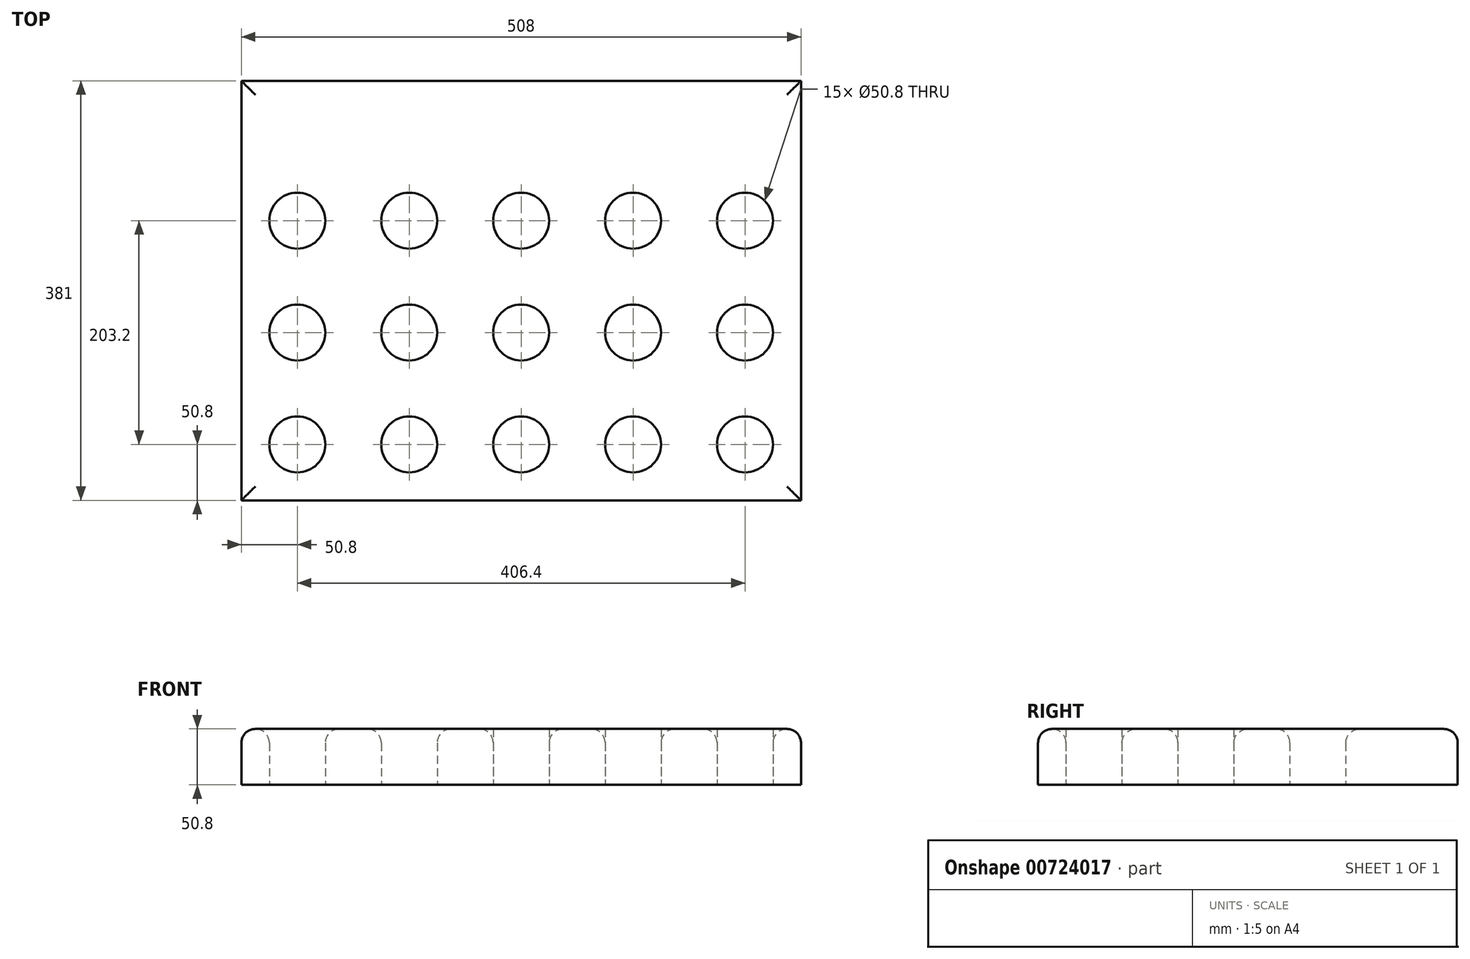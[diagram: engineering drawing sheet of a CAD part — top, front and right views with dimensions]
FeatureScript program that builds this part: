
annotation { "Feature Type Name" : "Feature", "Feature Type Description" : "" }
export const myFeature = defineFeature(function(context is Context, id is Id, definition is map)
    precondition{}
    {
        {
            var Q0;
            Q0=qCreatedBy(makeId("Top.planeOp"),FACE);
            var sketch = newSketch(context, id + "F0", { "sketchPlane" : qUnion([Q0])});
            skLineSegment(sketch, "E0.bottom", {"start": v(254, -190.5) * mm, "end": v(-254, -190.5) * mm});
            skLineSegment(sketch, "E0.top", {"start": v(254, 190.5) * mm, "end": v(-254, 190.5) * mm});
            skLineSegment(sketch, "E0.left", {"start": v(254, -190.5) * mm, "end": v(254, 190.5) * mm});
            skLineSegment(sketch, "E0.right", {"start": v(-254, -190.5) * mm, "end": v(-254, 190.5) * mm});
            skPoint(sketch, "E0.middle", {"position": v(0, 0) * mm});
            skLineSegment(sketch, "E1.bottom", {"start": v(-381, -190.5) * mm, "end": v(-431.8, -190.5) * mm});
            skLineSegment(sketch, "E1.top", {"start": v(-381, -266.7) * mm, "end": v(-431.8, -266.7) * mm});
            skLineSegment(sketch, "E1.left", {"start": v(-381, -190.5) * mm, "end": v(-381, -266.7) * mm});
            skLineSegment(sketch, "E1.right", {"start": v(-431.8, -190.5) * mm, "end": v(-431.8, -266.7) * mm});
            skPoint(sketch, "E1.middle", {"position": v(-406.4, -228.6) * mm});
            skCircle(sketch, "E2", {"center": v(-203.2, -139.7) * mm, "radius": 25.4 * mm});
            skCircle(sketch, "E3.0.1.0", {"center": v(-203.2, -38.1) * mm, "radius": 25.4 * mm});
            skCircle(sketch, "E3.0.2.0", {"center": v(-203.2, 63.5) * mm, "radius": 25.4 * mm});
            skCircle(sketch, "E3.1.0.0", {"center": v(-101.6, -139.7) * mm, "radius": 25.4 * mm});
            skCircle(sketch, "E3.1.1.0", {"center": v(-101.6, -38.1) * mm, "radius": 25.4 * mm});
            skCircle(sketch, "E3.1.2.0", {"center": v(-101.6, 63.5) * mm, "radius": 25.4 * mm});
            skCircle(sketch, "E3.2.0.0", {"center": v(0, -139.7) * mm, "radius": 25.4 * mm});
            skCircle(sketch, "E3.2.1.0", {"center": v(0, -38.1) * mm, "radius": 25.4 * mm});
            skCircle(sketch, "E3.2.2.0", {"center": v(0, 63.5) * mm, "radius": 25.4 * mm});
            skCircle(sketch, "E3.3.0.0", {"center": v(101.6, -139.7) * mm, "radius": 25.4 * mm});
            skCircle(sketch, "E3.3.1.0", {"center": v(101.6, -38.1) * mm, "radius": 25.4 * mm});
            skCircle(sketch, "E3.3.2.0", {"center": v(101.6, 63.5) * mm, "radius": 25.4 * mm});
            skCircle(sketch, "E3.4.0.0", {"center": v(203.2, -139.7) * mm, "radius": 25.4 * mm});
            skCircle(sketch, "E3.4.1.0", {"center": v(203.2, -38.1) * mm, "radius": 25.4 * mm});
            skCircle(sketch, "E3.4.2.0", {"center": v(203.2, 63.5) * mm, "radius": 25.4 * mm});
            skLineSegment(sketch, "E3.direction1", {"start": v(-203.2, -139.7) * mm, "end": v(-101.6, -139.7) * mm, "construction": true});
            skLineSegment(sketch, "E3.direction2", {"start": v(-203.2, -139.7) * mm, "end": v(-203.2, -38.1) * mm, "construction": true});
            skSolve(sketch);
        }
        {
            var Q0;
            Q0=makeQuery(id+"F0.imprint","IMPRINT",FACE,{"disambiguationData":[TD([[makeQuery(id+"F0.imprint","IMPRINT",EDGE,{"derivedFrom":sQuery(id+"F0.wireOp",EDGE,"E0.bottom")}),-1.0]])]});
            extrude(context, id + "F1", {"entities" : qUnion([Q0]), "depth" : 50.8 * mm, "offsetDistance" : 25.4 * mm});
        }
        {
            var Q0;
            Q0=makeQuery(id+"F1.opExtrude","CAP_EDGE",EDGE,{"disambiguationData":[OSD([sQuery(id+"F0.wireOp",EDGE,"E0.right")])],"isStart":false});
            var Q1;
            Q1=makeQuery(id+"F1.opExtrude","CAP_EDGE",EDGE,{"disambiguationData":[OSD([sQuery(id+"F0.wireOp",EDGE,"E0.bottom")])],"isStart":false});
            var Q2;
            Q2=makeQuery(id+"F1.opExtrude","CAP_EDGE",EDGE,{"disambiguationData":[OSD([sQuery(id+"F0.wireOp",EDGE,"E0.top")])],"isStart":false});
            var Q3;
            Q3=makeQuery(id+"F1.opExtrude","CAP_EDGE",EDGE,{"disambiguationData":[OSD([sQuery(id+"F0.wireOp",EDGE,"E0.left")])],"isStart":false});
            var Q4;
            Q4=makeQuery(id+"F1.opExtrude","CAP_EDGE",EDGE,{"disambiguationData":[OSD([sQuery(id+"F0.wireOp",EDGE,"E3.4.2.0")])],"isStart":false});
            var Q5;
            Q5=makeQuery(id+"F1.opExtrude","CAP_EDGE",EDGE,{"disambiguationData":[OSD([sQuery(id+"F0.wireOp",EDGE,"E3.3.2.0")])],"isStart":false});
            var Q6;
            Q6=makeQuery(id+"F1.opExtrude","CAP_EDGE",EDGE,{"disambiguationData":[OSD([sQuery(id+"F0.wireOp",EDGE,"E3.2.2.0")])],"isStart":false});
            var Q7;
            Q7=makeQuery(id+"F1.opExtrude","CAP_EDGE",EDGE,{"disambiguationData":[OSD([sQuery(id+"F0.wireOp",EDGE,"E3.1.2.0")])],"isStart":false});
            var Q8;
            Q8=makeQuery(id+"F1.opExtrude","CAP_EDGE",EDGE,{"disambiguationData":[OSD([sQuery(id+"F0.wireOp",EDGE,"E3.0.2.0")])],"isStart":false});
            var Q9;
            Q9=makeQuery(id+"F1.opExtrude","CAP_EDGE",EDGE,{"disambiguationData":[OSD([sQuery(id+"F0.wireOp",EDGE,"E3.0.1.0")])],"isStart":false});
            var Q10;
            Q10=makeQuery(id+"F1.opExtrude","CAP_EDGE",EDGE,{"disambiguationData":[OSD([sQuery(id+"F0.wireOp",EDGE,"E2")])],"isStart":false});
            var Q11;
            Q11=makeQuery(id+"F1.opExtrude","CAP_EDGE",EDGE,{"disambiguationData":[OSD([sQuery(id+"F0.wireOp",EDGE,"E3.1.0.0")])],"isStart":false});
            var Q12;
            Q12=makeQuery(id+"F1.opExtrude","CAP_EDGE",EDGE,{"disambiguationData":[OSD([sQuery(id+"F0.wireOp",EDGE,"E3.1.1.0")])],"isStart":false});
            var Q13;
            Q13=makeQuery(id+"F1.opExtrude","CAP_EDGE",EDGE,{"disambiguationData":[OSD([sQuery(id+"F0.wireOp",EDGE,"E3.2.1.0")])],"isStart":false});
            fillet(context, id + "F2", {"entities" : qUnion([Q0, Q1, Q2, Q3, Q4, Q5, Q6, Q7, Q8, Q9, Q10, Q11, Q12, Q13]), "radius" : 12.7 * mm, "tangentPropagation" : true, "allowEdgeOverflow" : false});
        }
    });
